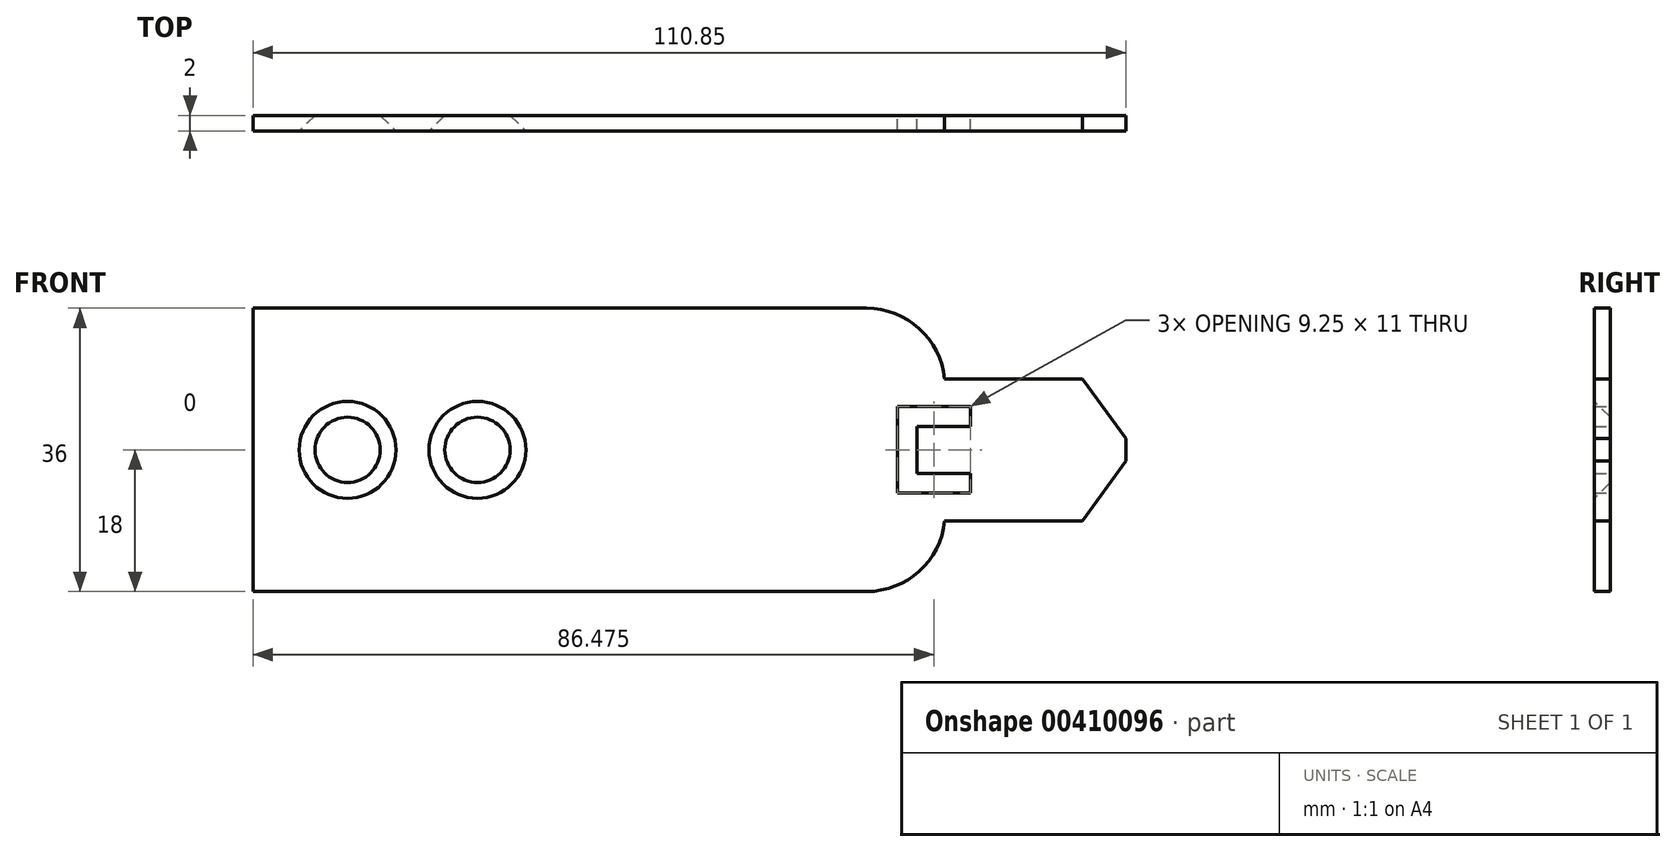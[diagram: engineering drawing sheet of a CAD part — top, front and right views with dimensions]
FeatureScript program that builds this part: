
annotation { "Feature Type Name" : "Feature", "Feature Type Description" : "" }
export const myFeature = defineFeature(function(context is Context, id is Id, definition is map)
    precondition{}
    {
        {
            var Q0;
            Q0=qCreatedBy(makeId("Front.planeOp"),FACE);
            var sketch = newSketch(context, id + "F0", { "sketchPlane" : qUnion([Q0])});
            skLineSegment(sketch, "E0", {"start": v(0, 18) * mm, "end": v(0, -18) * mm});
            skLineSegment(sketch, "E1", {"start": v(0, 18) * mm, "end": v(87.85, 18) * mm});
            skLineSegment(sketch, "E2", {"start": v(87.85, 18) * mm, "end": v(87.85, 9) * mm});
            skLineSegment(sketch, "E3", {"start": v(87.85, 9) * mm, "end": v(105.35, 9) * mm});
            skLineSegment(sketch, "E4", {"start": v(105.35, 9) * mm, "end": v(110.85, 1.42) * mm});
            skLineSegment(sketch, "E5", {"start": v(110.85, 1.42) * mm, "end": v(110.85, -1.42) * mm});
            skLineSegment(sketch, "E6", {"start": v(0, 0) * mm, "end": v(110.85, 0) * mm, "construction": true});
            skLineSegment(sketch, "E7.MirrorCS", {"start": v(0, -18) * mm, "end": v(87.85, -18) * mm});
            skLineSegment(sketch, "E8.MirrorCS", {"start": v(87.85, -18) * mm, "end": v(87.85, -9) * mm});
            skLineSegment(sketch, "E9.MirrorCS", {"start": v(87.85, -9) * mm, "end": v(105.35, -9) * mm});
            skLineSegment(sketch, "E10.MirrorCS", {"start": v(105.35, -9) * mm, "end": v(110.85, -1.42) * mm});
            skCircle(sketch, "E11", {"center": v(12, 0) * mm, "radius": 4.15 * mm});
            skCircle(sketch, "E12", {"center": v(28.5, 0) * mm, "radius": 4.15 * mm});
            skLineSegment(sketch, "E13.bottom", {"start": v(91.1, 3) * mm, "end": v(84.35, 3) * mm});
            skLineSegment(sketch, "E13.top", {"start": v(91.1, -3) * mm, "end": v(84.35, -3) * mm});
            skLineSegment(sketch, "E13.right", {"start": v(84.35, 3) * mm, "end": v(84.35, -3) * mm});
            skLineSegment(sketch, "E14.0", {"start": v(91.1, -5.5) * mm, "end": v(81.85, -5.5) * mm});
            skLineSegment(sketch, "E14.1", {"start": v(81.85, 5.5) * mm, "end": v(81.85, -5.5) * mm});
            skLineSegment(sketch, "E14.2", {"start": v(91.1, 5.5) * mm, "end": v(81.85, 5.5) * mm});
            skLineSegment(sketch, "E15", {"start": v(91.1, 5.5) * mm, "end": v(91.1, 3) * mm});
            skLineSegment(sketch, "E16", {"start": v(91.1, -3) * mm, "end": v(91.1, -5.5) * mm});
            skSolve(sketch);
        }
        {
            var Q0;
            Q0 = qSketchRegion(id + "F0", true);
            extrude(context, id + "F1", {"entities" : qUnion([Q0]), "depth" : 2 * mm});
        }
        {
            var Q0;
            Q0=makeQuery(id+"F1.opExtrude","CAP_EDGE",EDGE,{"disambiguationData":[OSD([sQuery(id+"F0.wireOp",EDGE,"E11")])],"isStart":false});
            var Q1;
            Q1=makeQuery(id+"F1.opExtrude","CAP_EDGE",EDGE,{"disambiguationData":[OSD([sQuery(id+"F0.wireOp",EDGE,"E12")])],"isStart":false});
            chamfer(context, id + "F2", {"entities" : qUnion([Q0, Q1]), "width" : 2 * mm, "tangentPropagation" : true});
        }
        {
            var Q0;
            Q0=makeQuery(id+"F1.opExtrude","SWEPT_EDGE",EDGE,{"disambiguationData":[OSD([sQuery(id+"F0.wireOp",EDGE,"E1"),sQuery(id+"F0.wireOp",EDGE,"E2")])]});
            var Q1;
            Q1=makeQuery(id+"F1.opExtrude","SWEPT_EDGE",EDGE,{"disambiguationData":[OSD([sQuery(id+"F0.wireOp",EDGE,"E7.MirrorCS"),sQuery(id+"F0.wireOp",EDGE,"E8.MirrorCS")])]});
            fillet(context, id + "F3", {"entities" : qUnion([Q0, Q1]), "radius" : 10 * mm, "tangentPropagation" : true, "allowEdgeOverflow" : false});
        }
    });
